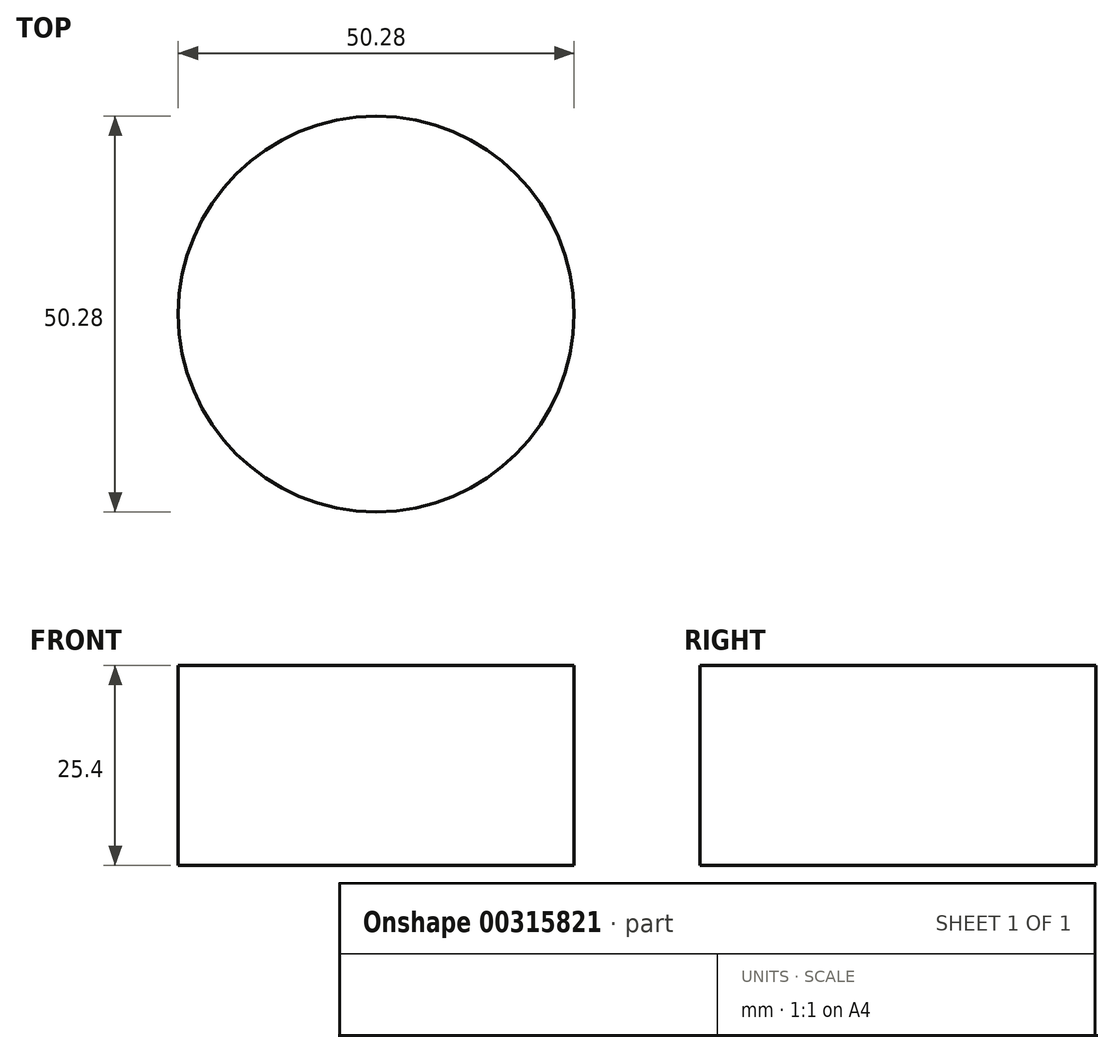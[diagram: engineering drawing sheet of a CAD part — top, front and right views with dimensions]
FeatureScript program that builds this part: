
annotation { "Feature Type Name" : "Feature", "Feature Type Description" : "" }
export const myFeature = defineFeature(function(context is Context, id is Id, definition is map)
    precondition{}
    {
        {
            var Q0;
            Q0=qCreatedBy(makeId("Top.planeOp"),FACE);
            var sketch = newSketch(context, id + "F0", { "sketchPlane" : qUnion([Q0])});
            skCircle(sketch, "E0", {"center": v(0, 0) * mm, "radius": 25.14 * mm});
            skSolve(sketch);
        }
        {
            var Q0;
            Q0=sQuery(id+"F0.wireOp",EDGE,"E0");
            extrude(context, id + "F1", {"bodyType" : ToolBodyType.SURFACE, "surfaceEntities" : qUnion([Q0]), "depth" : 25.4 * mm});
        }
    });
